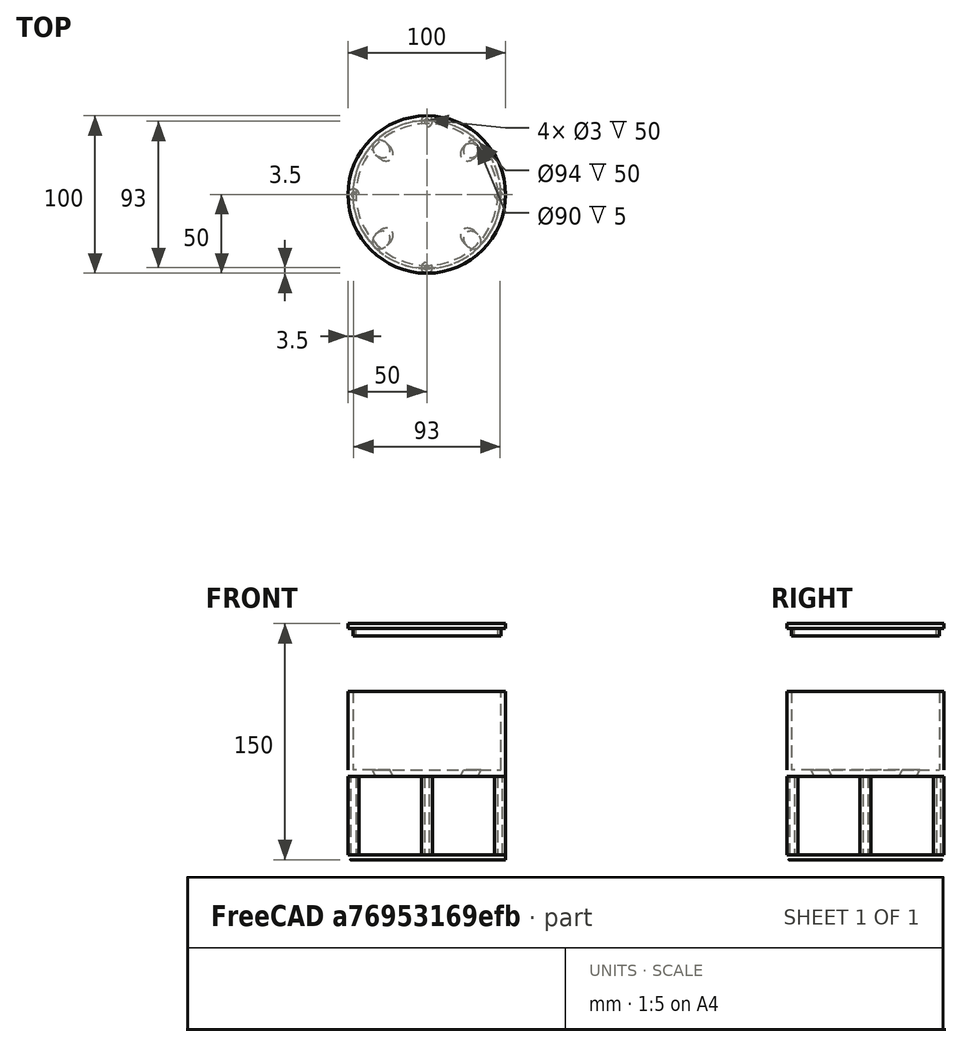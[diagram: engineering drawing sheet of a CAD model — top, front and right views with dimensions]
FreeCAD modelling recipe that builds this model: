
FCSTD DOCUMENT  (FreeCAD 0.21Rpre_30265.fc36 (Git))
Label: FabWindy
License: All rights reserved
LicenseURL: https://en.wikipedia.org/wiki/All_rights_reserved
objects: Sketcher::SketchObject×10, PartDesign::Pad×6, PartDesign::Plane×4, PartDesign::Pocket×4, PartDesign::Body×2, Spreadsheet::Sheet×1, PartDesign::PolarPattern×1, PartDesign::ShapeBinder×1
note: 38 computed .brp shape members not serialized (recipe doc carries the construction recipe); baked Part::Feature solids carry a one-line shape summary decoded from their .brp

FEATURE [Spreadsheet::Sheet] Spreadsheet
  cells = A3=Outer Diameter; B3(OuterDiameter)=100; A4=Top Height; B4(TopHeight)=50; A5=WindTunnelHeight; B5(WindTunnelHeight)=50; A6=WindTunnelBaseThickness; B6(WindTunnelBaseHeight)=3; A7=TransducerAngle; B7(TransducerAngle)=35; A8=TransducerDatumZ; B8(TransducerDatumZ)=33
FEATURE [Sketcher::SketchObject] Sketch
  FullyConstrained = true
  MapMode = 5
  Support = -> [XY_Plane]
  expr: Constraints[1] = <<Spreadsheet>>.OuterDiameter
  sketch-geometry (1):
    g0: Circle CenterX=0 CenterY=0 CenterZ=0 NormalX=0 NormalY=0 NormalZ=1 AngleXU=0 Radius=50
  constraints (2):
    c: Coincident(g0,g-1)
    c: Diameter(g0) = 100
FEATURE [PartDesign::Pad] Pad
  Direction = (0,0,1)
  Length = 3
  Length2 = 10
  Profile = -> Sketch
  ReferenceAxis = -> Sketch [N_Axis]
  Type = 0
  expr: Length = <<Spreadsheet>>.WindTunnelBaseHeight
FEATURE [Sketcher::SketchObject] Sketch001
  ExternalGeometry = -> [Pad]
  FullyConstrained = true
  MapMode = 5
  Placement = pos=(0,0,3) rot=(0,0,1;0rad)
  Support = -> [Pad]
  sketch-geometry (3):
    g0: Circle CenterX=46.5 CenterY=0 CenterZ=0 NormalX=0 NormalY=0 NormalZ=1 AngleXU=0 Radius=3.5
    g1: Circle CenterX=46.5 CenterY=0 CenterZ=0 NormalX=0 NormalY=0 NormalZ=1 AngleXU=0 Radius=1.5
    g2: LineSegment StartX=46.5 StartY=-1.5 StartZ=0 EndX=46.5 EndY=-3.5 EndZ=0
  constraints (9):
    c: PointOnObject(g1,g-1)
    c: Coincident(g0,g1)
    c: PointOnObject(g2,g1)
    c: PointOnObject(g2,g0)
    c: Perpendicular(g1,g2)
    c: Distance(g2) = 2
    c: Vertical(g2)
    c: Diameter(g0) = 7
    c: Tangent(g0,g-3)
FEATURE [PartDesign::Pad] Pad001
  BaseFeature = -> Pad
  Direction = (0,0,1)
  Length = 50
  Length2 = 10
  Profile = -> Sketch001
  ReferenceAxis = -> Sketch001 [N_Axis]
  Type = 0
  expr: Length = <<Spreadsheet>>.WindTunnelHeight
FEATURE [PartDesign::PolarPattern] PolarPattern
  Angle = 360
  Axis = -> Sketch001 [N_Axis]
  BaseFeature = -> Pad001
  Occurrences = 4
  Originals = -> [Pad001]
FEATURE [Sketcher::SketchObject] Sketch002
  FullyConstrained = true
  MapMode = 5
  Placement = pos=(0,0,53) rot=(0,0,1;0rad)
  Support = -> [PolarPattern]
  expr: Constraints[1] = <<Spreadsheet>>.OuterDiameter
  sketch-geometry (1):
    g0: Circle CenterX=0 CenterY=0 CenterZ=0 NormalX=0 NormalY=0 NormalZ=1 AngleXU=0 Radius=50
  constraints (2):
    c: Coincident(g0,g-1)
    c: Diameter(g0) = 100
FEATURE [PartDesign::Pad] Pad002
  BaseFeature = -> PolarPattern
  Direction = (0,0,1)
  Length = 4
  Length2 = 10
  Profile = -> Sketch002
  ReferenceAxis = -> Sketch002 [N_Axis]
  Type = 0
FEATURE [Sketcher::SketchObject] Sketch003
  ExternalGeometry = -> [Pad002]
  FullyConstrained = true
  MapMode = 5
  Placement = pos=(0,0,57) rot=(0,0,1;0rad)
  Support = -> [Pad002]
  sketch-geometry (3):
    g0: Circle CenterX=0 CenterY=0 CenterZ=0 NormalX=0 NormalY=0 NormalZ=1 AngleXU=0 Radius=50
    g1: Circle CenterX=0 CenterY=0 CenterZ=0 NormalX=0 NormalY=0 NormalZ=1 AngleXU=0 Radius=47
    g2: LineSegment StartX=47 StartY=0 StartZ=0 EndX=50 EndY=0 EndZ=0
  constraints (8):
    c: Coincident(g0,g-1)
    c: Coincident(g1,g0)
    c: Equal(g0,g-3)
    c: PointOnObject(g2,g1)
    c: PointOnObject(g2,g0)
    c: Perpendicular(g1,g2)
    c: Distance(g2) = 3
    c: Horizontal(g2)
FEATURE [PartDesign::Pad] Pad003
  BaseFeature = -> Pad002
  Direction = (0,0,1)
  Length = 50
  Length2 = 10
  Profile = -> Sketch003
  ReferenceAxis = -> Sketch003 [N_Axis]
  Type = 0
  expr: Length = <<Spreadsheet>>.TopHeight
FEATURE [Sketcher::SketchObject] Sketch004
  FullyConstrained = true
  MapMode = 5
  Support = -> [XY_Plane001]
  expr: Constraints[1] = <<Spreadsheet>>.OuterDiameter
  sketch-geometry (1):
    g0: Circle CenterX=0 CenterY=0 CenterZ=0 NormalX=0 NormalY=0 NormalZ=1 AngleXU=0 Radius=50
  constraints (2):
    c: Coincident(g0,g-1)
    c: Diameter(g0) = 100
FEATURE [PartDesign::Pad] Pad004
  Direction = (0,0,1)
  Length = 3
  Length2 = 10
  Profile = -> Sketch004
  ReferenceAxis = -> Sketch004 [N_Axis]
  Type = 0
FEATURE [PartDesign::ShapeBinder] ShapeBinder
  Support = -> [Sketch003]
  TraceSupport = false
FEATURE [Sketcher::SketchObject] Sketch005
  ExternalGeometry = -> [ShapeBinder]
  FullyConstrained = true
  MapMode = 5
  Placement = pos=(0,0,3) rot=(0,0,1;0rad)
  Support = -> [Pad004]
  sketch-geometry (3):
    g0: Circle CenterX=0 CenterY=0 CenterZ=0 NormalX=0 NormalY=0 NormalZ=1 AngleXU=0 Radius=47
    g1: Circle CenterX=0 CenterY=0 CenterZ=0 NormalX=0 NormalY=0 NormalZ=1 AngleXU=0 Radius=45
    g2: LineSegment StartX=45 StartY=0 StartZ=0 EndX=47 EndY=0 EndZ=0
  constraints (7):
    c: Coincident(g0,g-3)
    c: Equal(g0,g-3)
    c: Coincident(g1,g0)
    c: PointOnObject(g2,g1)
    c: PointOnObject(g2,g0)
    c: DistanceX(g2,g2) = 2
    c: Tangent(g2,g-1)
FEATURE [PartDesign::Pad] Pad005
  BaseFeature = -> Pad004
  Direction = (0,0,1)
  Length = 5
  Length2 = 10
  Profile = -> Sketch005
  ReferenceAxis = -> Sketch005 [N_Axis]
  Type = 0
FEATURE [PartDesign::Body] Body001  label="Cap"
  Group = -> [Sketch004,Pad004,ShapeBinder,Sketch005,Pad005]
  Origin = -> Origin001
  Placement = pos=(0,0,150) rot=(1,0,0;3.14159rad)
  Tip = -> Pad005
FEATURE [PartDesign::Plane] DatumPlane
  AttachmentOffset = pos=(0,0,33) rot=(-0.243343,0.587481,0.771784;0.985144rad)
  Length = 224.476
  MapMode = 5
  Placement = pos=(0,0,90) rot=(-0.243343,0.587481,0.771784;0.985144rad)
  ResizeMode = 0
  Support = -> [Pad003]
  Width = 174.34
  expr: .AttachmentOffset.Base.z = <<Spreadsheet>>.TransducerDatumZ
  expr: .AttachmentOffset.Rotation.Pitch = <<Spreadsheet>>.TransducerAngle
FEATURE [Sketcher::SketchObject] Sketch007
  ExternalGeometry = -> [Sketch003]
  FullyConstrained = true
  MapMode = 5
  Placement = pos=(0,0,90) rot=(-0.243343,0.587481,0.771784;0.985144rad)
  Support = -> [DatumPlane]
  sketch-geometry (2):
    g0: Circle CenterX=52.4282 CenterY=0 CenterZ=0 NormalX=0 NormalY=0 NormalZ=1 AngleXU=0 Radius=5
    g1: GeomPoint X=57.4282 Y=-1e-16 Z=0
  constraints (5):
    c: PointOnObject(g0,g-1)
    c: Diameter(g0) = 10
    c: PointOnObject(g1,g-3)
    c: PointOnObject(g1,g0)
    c: Tangent(g-3,g0,g1) = -1.5708
FEATURE [PartDesign::Pocket] Pocket
  BaseFeature = -> Pad003
  Direction = (-0.40558,-0.40558,-0.819152)
  Length = 15
  Length2 = 5
  Profile = -> Sketch007
  ReferenceAxis = -> Sketch007 [N_Axis]
  Type = 0
FEATURE [PartDesign::Plane] DatumPlane001
  AttachmentOffset = pos=(0,0,33) rot=(0.587481,0.243343,0.771784;0.985144rad)
  Length = 174.34
  MapMode = 5
  Placement = pos=(0,0,90) rot=(0.587481,0.243343,0.771784;0.985144rad)
  ResizeMode = 0
  Support = -> [Pad003]
  Width = 224.476
  expr: .AttachmentOffset.Base.z = <<Spreadsheet>>.TransducerDatumZ
  expr: .AttachmentOffset.Rotation.Roll = <<Spreadsheet>>.TransducerAngle
FEATURE [Sketcher::SketchObject] Sketch008
  ExternalGeometry = -> [Sketch003]
  FullyConstrained = true
  MapMode = 5
  Placement = pos=(0,0,90) rot=(0.587481,0.243343,0.771784;0.985144rad)
  Support = -> [DatumPlane001]
  sketch-geometry (2):
    g0: Circle CenterX=0 CenterY=-52.4282 CenterZ=0 NormalX=0 NormalY=0 NormalZ=1 AngleXU=0 Radius=5
    g1: GeomPoint X=0 Y=-57.4282 Z=0
  constraints (5):
    c: Diameter(g0) = 10
    c: PointOnObject(g0,g-2)
    c: PointOnObject(g1,g-3)
    c: PointOnObject(g1,g0)
    c: Tangent(g-3,g0,g1) = -1.5708
FEATURE [PartDesign::Pocket] Pocket001
  BaseFeature = -> Pocket
  Direction = (-0.40558,0.40558,-0.819152)
  Length = 15
  Length2 = 5
  Profile = -> Sketch008
  ReferenceAxis = -> Sketch008 [N_Axis]
  Type = 0
FEATURE [PartDesign::Plane] DatumPlane002
  AttachmentOffset = pos=(0,0,33) rot=(0.587481,-0.243343,-0.771784;0.985144rad)
  Length = 174.34
  MapMode = 5
  Placement = pos=(0,0,90) rot=(0.587481,-0.243343,-0.771784;0.985144rad)
  ResizeMode = 0
  Support = -> [Pad003]
  Width = 224.476
  expr: .AttachmentOffset.Base.z = <<Spreadsheet>>.TransducerDatumZ
  expr: .AttachmentOffset.Rotation.Roll = <<Spreadsheet>>.TransducerAngle
FEATURE [Sketcher::SketchObject] Sketch009
  ExternalGeometry = -> [Sketch003]
  FullyConstrained = true
  MapMode = 5
  Placement = pos=(0,0,90) rot=(0.587481,-0.243343,-0.771784;0.985144rad)
  Support = -> [DatumPlane002]
  sketch-geometry (2):
    g0: Circle CenterX=0 CenterY=-52.4282 CenterZ=0 NormalX=0 NormalY=0 NormalZ=1 AngleXU=0 Radius=5
    g1: GeomPoint X=0 Y=-57.4282 Z=0
  constraints (5):
    c: PointOnObject(g0,g-2)
    c: Diameter(g0) = 10
    c: PointOnObject(g1,g-3)
    c: PointOnObject(g1,g0)
    c: Tangent(g-3,g0,g1) = -1.5708
FEATURE [PartDesign::Pocket] Pocket002
  BaseFeature = -> Pocket001
  Direction = (0.40558,0.40558,-0.819152)
  Length = 15
  Length2 = 5
  Profile = -> Sketch009
  ReferenceAxis = -> Sketch009 [N_Axis]
  Type = 0
FEATURE [PartDesign::Plane] DatumPlane003
  AttachmentOffset = pos=(0,0,33) rot=(0.123601,-0.2984,-0.946404;2.39439rad)
  Length = 174.34
  MapMode = 5
  Placement = pos=(0,0,90) rot=(0.123601,-0.2984,-0.946404;2.39439rad)
  ResizeMode = 0
  Support = -> [Pad003]
  Width = 224.476
  expr: .AttachmentOffset.Base.z = <<Spreadsheet>>.TransducerDatumZ
  expr: .AttachmentOffset.Rotation.Roll = <<Spreadsheet>>.TransducerAngle
FEATURE [Sketcher::SketchObject] Sketch010
  ExternalGeometry = -> [Sketch003]
  FullyConstrained = true
  MapMode = 5
  Placement = pos=(0,0,90) rot=(-0.123601,0.2984,0.946404;3.8888rad)
  Support = -> [DatumPlane003]
  sketch-geometry (2):
    g0: Circle CenterX=0 CenterY=-52.4282 CenterZ=0 NormalX=0 NormalY=0 NormalZ=1 AngleXU=0 Radius=5
    g1: GeomPoint X=0 Y=-57.4282 Z=0
  constraints (5):
    c: PointOnObject(g0,g-2)
    c: Diameter(g0) = 10
    c: PointOnObject(g1,g-3)
    c: PointOnObject(g1,g0)
    c: Tangent(g-3,g0,g1) = -1.5708
FEATURE [PartDesign::Pocket] Pocket003
  BaseFeature = -> Pocket002
  Direction = (0.40558,-0.40558,-0.819152)
  Length = 15
  Length2 = 5
  Profile = -> Sketch010
  ReferenceAxis = -> Sketch010 [N_Axis]
  Type = 0
FEATURE [PartDesign::Body] Body
  Group = -> [Sketch,Pad,Sketch001,Pad001,PolarPattern,Sketch002,Pad002,Sketch003,Pad003,DatumPlane,Sketch007,Pocket,DatumPlane001,Sketch008,Pocket001,DatumPlane002,Sketch009,Pocket002,DatumPlane003,Sketch010,Pocket003]
  Origin = -> Origin
  Tip = -> Pocket003
